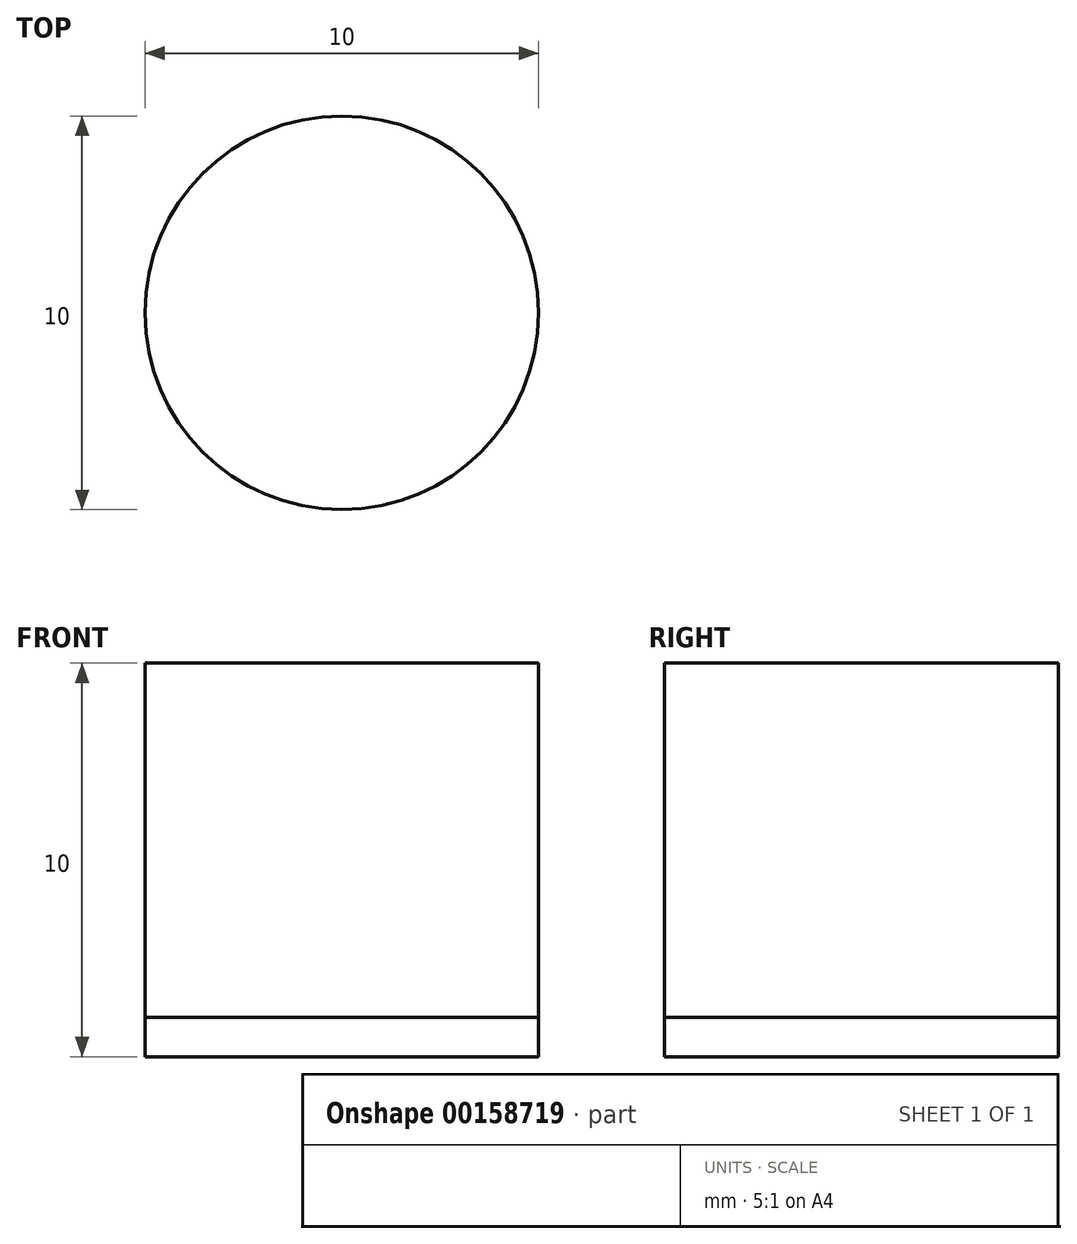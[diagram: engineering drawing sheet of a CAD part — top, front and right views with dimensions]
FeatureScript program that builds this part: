
annotation { "Feature Type Name" : "Feature", "Feature Type Description" : "" }
export const myFeature = defineFeature(function(context is Context, id is Id, definition is map)
    precondition{}
    {
        {
            var Q0;
            Q0=qCreatedBy(makeId("Top.planeOp"),FACE);
            var sketch = newSketch(context, id + "F0", { "sketchPlane" : qUnion([Q0])});
            skLineSegment(sketch, "E0.bottom", {"start": v(33, 33) * mm, "end": v(-33, 33) * mm});
            skLineSegment(sketch, "E0.top", {"start": v(33, -33) * mm, "end": v(-33, -33) * mm});
            skLineSegment(sketch, "E0.left", {"start": v(33, 33) * mm, "end": v(33, -33) * mm});
            skLineSegment(sketch, "E0.right", {"start": v(-33, 33) * mm, "end": v(-33, -33) * mm});
            skPoint(sketch, "E0.middle", {"position": v(0, 0) * mm});
            skCircle(sketch, "E1", {"center": v(-33, 33) * mm, "radius": 5 * mm});
            skCircle(sketch, "E2", {"center": v(-33, 33) * mm, "radius": 13 * mm});
            skCircle(sketch, "E3.0", {"center": v(-33, 33) * mm, "radius": 9 * mm});
            skCircle(sketch, "E4.0.1.0", {"center": v(-33, -33) * mm, "radius": 13 * mm});
            skCircle(sketch, "E4.0.1.1", {"center": v(-33, -33) * mm, "radius": 9 * mm});
            skCircle(sketch, "E4.0.1.2", {"center": v(-33, -33) * mm, "radius": 5 * mm});
            skCircle(sketch, "E4.1.0.0", {"center": v(33, 33) * mm, "radius": 13 * mm});
            skCircle(sketch, "E4.1.0.1", {"center": v(33, 33) * mm, "radius": 9 * mm});
            skCircle(sketch, "E4.1.0.2", {"center": v(33, 33) * mm, "radius": 5 * mm});
            skCircle(sketch, "E4.1.1.0", {"center": v(33, -33) * mm, "radius": 13 * mm});
            skCircle(sketch, "E4.1.1.1", {"center": v(33, -33) * mm, "radius": 9 * mm});
            skCircle(sketch, "E4.1.1.2", {"center": v(33, -33) * mm, "radius": 5 * mm});
            skLineSegment(sketch, "E4.direction1", {"start": v(-33, 33) * mm, "end": v(33, 33) * mm, "construction": true});
            skLineSegment(sketch, "E4.direction2", {"start": v(-33, 33) * mm, "end": v(-33, -33) * mm, "construction": true});
            skSolve(sketch);
        }
        {
            var Q0;
            {var subQ0=sQuery(id+"F0.wireOp",EDGE,"E2");var subQ1=sQuery(id+"F0.wireOp",EDGE,"E0.bottom");var subQ2=makeQuery(id+"F0.imprint","INTERSECT",VERTEX,{"derivedFrom":[subQ1,subQ0]});Q0=makeQuery(id+"F0.imprint","IMPRINT",FACE,{"disambiguationData":[TD([[makeQuery(id+"F0.imprint","IMPRINT",EDGE,{"disambiguationData":[TD([[subQ2,-1.0]])],"derivedFrom":subQ1}),-1.0]])]});}
            var Q1;
            {var subQ0=sQuery(id+"F0.wireOp",EDGE,"E2");var subQ1=sQuery(id+"F0.wireOp",EDGE,"E0.bottom");var subQ2=makeQuery(id+"F0.imprint","INTERSECT",VERTEX,{"derivedFrom":[subQ1,subQ0]});Q1=makeQuery(id+"F0.imprint","IMPRINT",FACE,{"disambiguationData":[TD([[makeQuery(id+"F0.imprint","IMPRINT",EDGE,{"disambiguationData":[TD([[subQ2,-1.0]])],"derivedFrom":subQ1}),1.0]])]});}
            extrude(context, id + "F1", {"entities" : qUnion([Q0, Q1]), "endBound" : BoundingType.SYMMETRIC, "depth" : 20 * mm});
        }
        {
            var Q0;
            {var subQ0=sQuery(id+"F0.wireOp",EDGE,"E3.0");var subQ1=sQuery(id+"F0.wireOp",EDGE,"E0.bottom");var subQ2=makeQuery(id+"F0.imprint","INTERSECT",VERTEX,{"derivedFrom":[subQ1,subQ0]});Q0=makeQuery(id+"F0.imprint","IMPRINT",FACE,{"disambiguationData":[TD([[makeQuery(id+"F0.imprint","IMPRINT",EDGE,{"disambiguationData":[TD([[subQ2,-1.0]])],"derivedFrom":subQ1}),-1.0]])]});}
            var Q1;
            {var subQ0=sQuery(id+"F0.wireOp",EDGE,"E3.0");var subQ1=sQuery(id+"F0.wireOp",EDGE,"E0.bottom");var subQ2=makeQuery(id+"F0.imprint","INTERSECT",VERTEX,{"derivedFrom":[subQ1,subQ0]});Q1=makeQuery(id+"F0.imprint","IMPRINT",FACE,{"disambiguationData":[TD([[makeQuery(id+"F0.imprint","IMPRINT",EDGE,{"disambiguationData":[TD([[subQ2,-1.0]])],"derivedFrom":subQ1}),1.0]])]});}
            extrude(context, id + "F2", {"entities" : qUnion([Q0, Q1]), "operationType" : NewBodyOperationType.ADD, "depth" : 5 * mm});
        }
        {
            var Q0;
            {var subQ0=sQuery(id+"F0.wireOp",EDGE,"E3.0");var subQ1=sQuery(id+"F0.wireOp",EDGE,"E0.bottom");var subQ2=makeQuery(id+"F0.imprint","INTERSECT",VERTEX,{"derivedFrom":[subQ1,subQ0]});Q0=makeQuery(id+"F0.imprint","IMPRINT",FACE,{"disambiguationData":[TD([[makeQuery(id+"F0.imprint","IMPRINT",EDGE,{"disambiguationData":[TD([[subQ2,-1.0]])],"derivedFrom":subQ1}),-1.0]])]});}
            var Q1;
            {var subQ0=sQuery(id+"F0.wireOp",EDGE,"E3.0");var subQ1=sQuery(id+"F0.wireOp",EDGE,"E0.bottom");var subQ2=makeQuery(id+"F0.imprint","INTERSECT",VERTEX,{"derivedFrom":[subQ1,subQ0]});Q1=makeQuery(id+"F0.imprint","IMPRINT",FACE,{"disambiguationData":[TD([[makeQuery(id+"F0.imprint","IMPRINT",EDGE,{"disambiguationData":[TD([[subQ2,-1.0]])],"derivedFrom":subQ1}),1.0]])]});}
            var Q2;
            Q2=makeQuery(id+"F1.opExtrude","CAP_FACE",FACE,{"disambiguationData":[OSD([sQuery(id+"F0.wireOp",EDGE,"E2"),sQuery(id+"F0.wireOp",EDGE,"E3.0")])],"isStart":true});
            extrude(context, id + "F3", {"entities" : qUnion([Q0, Q1]), "operationType" : NewBodyOperationType.ADD, "endBound" : BoundingType.UP_TO_SURFACE, "oppositeDirection" : true, "endBoundEntityFace" : qUnion([Q2]), "depth" : 10.25 * mm});
        }
        {
            var Q0;
            {var subQ0=sQuery(id+"F0.wireOp",EDGE,"E0.right");var subQ1=sQuery(id+"F0.wireOp",EDGE,"E0.bottom");var subQ2=makeQuery(id+"F0.imprint","INTERSECT",VERTEX,{"derivedFrom":[subQ1,subQ0]});Q0=makeQuery(id+"F0.imprint","IMPRINT",FACE,{"disambiguationData":[TD([[makeQuery(id+"F0.imprint","IMPRINT",EDGE,{"disambiguationData":[TD([[subQ2,1.0]])],"derivedFrom":subQ1}),-1.0]])]});}
            var Q1;
            {var subQ0=sQuery(id+"F0.wireOp",EDGE,"E0.right");var subQ1=sQuery(id+"F0.wireOp",EDGE,"E0.bottom");var subQ2=makeQuery(id+"F0.imprint","INTERSECT",VERTEX,{"derivedFrom":[subQ1,subQ0]});Q1=makeQuery(id+"F0.imprint","IMPRINT",FACE,{"disambiguationData":[TD([[makeQuery(id+"F0.imprint","IMPRINT",EDGE,{"disambiguationData":[TD([[subQ2,1.0]])],"derivedFrom":subQ1}),1.0]])]});}
            extrude(context, id + "F4", {"entities" : qUnion([Q0, Q1]), "operationType" : NewBodyOperationType.ADD, "depth" : 5 * mm});
        }
        {
            var Q0;
            {var subQ0=sQuery(id+"F0.wireOp",EDGE,"E0.right");var subQ1=sQuery(id+"F0.wireOp",EDGE,"E0.bottom");var subQ2=makeQuery(id+"F0.imprint","INTERSECT",VERTEX,{"derivedFrom":[subQ1,subQ0]});Q0=makeQuery(id+"F0.imprint","IMPRINT",FACE,{"disambiguationData":[TD([[makeQuery(id+"F0.imprint","IMPRINT",EDGE,{"disambiguationData":[TD([[subQ2,1.0]])],"derivedFrom":subQ1}),-1.0]])]});}
            var Q1;
            {var subQ0=sQuery(id+"F0.wireOp",EDGE,"E0.right");var subQ1=sQuery(id+"F0.wireOp",EDGE,"E0.bottom");var subQ2=makeQuery(id+"F0.imprint","INTERSECT",VERTEX,{"derivedFrom":[subQ1,subQ0]});Q1=makeQuery(id+"F0.imprint","IMPRINT",FACE,{"disambiguationData":[TD([[makeQuery(id+"F0.imprint","IMPRINT",EDGE,{"disambiguationData":[TD([[subQ2,1.0]])],"derivedFrom":subQ1}),1.0]])]});}
            extrude(context, id + "F5", {"entities" : qUnion([Q0, Q1]), "operationType" : NewBodyOperationType.ADD, "oppositeDirection" : true, "depth" : 9 * mm});
        }
        {
            var Q0;
            Q0=qCreatedBy(makeId("Top.planeOp"),FACE);
            var sketch = newSketch(context, id + "F6", { "sketchPlane" : qUnion([Q0])});
            skLineSegment(sketch, "E5.bottom", {"start": v(42, 42) * mm, "end": v(-42, 42) * mm});
            skLineSegment(sketch, "E5.top", {"start": v(42, -42) * mm, "end": v(-42, -42) * mm});
            skLineSegment(sketch, "E5.left", {"start": v(42, 42) * mm, "end": v(42, -42) * mm});
            skLineSegment(sketch, "E5.right", {"start": v(-42, 42) * mm, "end": v(-42, -42) * mm});
            skPoint(sketch, "E5.middle", {"position": v(0, 0) * mm});
            skFitSpline(sketch, "E6", {"points": [v(-42, 42) * mm, v(0, 48) * mm, v(42, 42) * mm], "startDerivative": vector(92.46, 24.65) * mm, "endDerivative": vector(96.06, -25.07) * mm});
            skFitSpline(sketch, "E7", {"points": [v(42, 42) * mm, v(48, 0) * mm, v(42, -42) * mm], "startDerivative": vector(24.84, -73.95) * mm, "endDerivative": vector(-21.58, -78.6) * mm});
            skFitSpline(sketch, "E8", {"points": [v(42, -42) * mm, v(0, -48) * mm, v(-42, -42) * mm], "startDerivative": vector(-77.44, -20.85) * mm, "endDerivative": vector(-75.53, 21.27) * mm});
            skFitSpline(sketch, "E9", {"points": [v(-42, -42) * mm, v(-48, 0) * mm, v(-42, 42) * mm], "startDerivative": vector(-24.73, 83.38) * mm, "endDerivative": vector(25.53, 85.94) * mm});
            skLineSegment(sketch, "E10.bottom", {"start": v(48, 48) * mm, "end": v(-48, 48) * mm});
            skLineSegment(sketch, "E10.top", {"start": v(48, -48) * mm, "end": v(-48, -48) * mm});
            skLineSegment(sketch, "E10.left", {"start": v(48, 48) * mm, "end": v(48, -48) * mm});
            skLineSegment(sketch, "E10.right", {"start": v(-48, 48) * mm, "end": v(-48, -48) * mm});
            skSolve(sketch);
        }
        {
            var Q0;
            Q0=qCreatedBy(makeId("Top.planeOp"),FACE);
            var sketch = newSketch(context, id + "F7", { "sketchPlane" : qUnion([Q0])});
            skLineSegment(sketch, "E11.bottom", {"start": v(28, 28) * mm, "end": v(-28, 28) * mm});
            skLineSegment(sketch, "E11.top", {"start": v(28, -28) * mm, "end": v(-28, -28) * mm});
            skLineSegment(sketch, "E11.left", {"start": v(28, 28) * mm, "end": v(28, -28) * mm});
            skLineSegment(sketch, "E11.right", {"start": v(-28, 28) * mm, "end": v(-28, -28) * mm});
            skPoint(sketch, "E11.middle", {"position": v(0, 0) * mm});
            skSolve(sketch);
        }
        {
            var Q0;
            {var subQ0=sQuery(id+"F0.wireOp",EDGE,"E4.1.0.0");var subQ1=sQuery(id+"F0.wireOp",EDGE,"E0.bottom");var subQ2=makeQuery(id+"F0.imprint","INTERSECT",VERTEX,{"derivedFrom":[subQ1,subQ0]});Q0=makeQuery(id+"F0.imprint","IMPRINT",FACE,{"disambiguationData":[TD([[makeQuery(id+"F0.imprint","IMPRINT",EDGE,{"disambiguationData":[TD([[subQ2,1.0]])],"derivedFrom":subQ1}),-1.0]])]});}
            var Q1;
            {var subQ0=sQuery(id+"F0.wireOp",EDGE,"E4.1.0.0");var subQ1=sQuery(id+"F0.wireOp",EDGE,"E0.bottom");var subQ2=makeQuery(id+"F0.imprint","INTERSECT",VERTEX,{"derivedFrom":[subQ1,subQ0]});Q1=makeQuery(id+"F0.imprint","IMPRINT",FACE,{"disambiguationData":[TD([[makeQuery(id+"F0.imprint","IMPRINT",EDGE,{"disambiguationData":[TD([[subQ2,1.0]])],"derivedFrom":subQ1}),1.0]])]});}
            extrude(context, id + "F8", {"entities" : qUnion([Q0, Q1]), "endBound" : BoundingType.SYMMETRIC, "depth" : 20 * mm});
        }
        {
            var Q0;
            {var subQ0=sQuery(id+"F0.wireOp",EDGE,"E4.1.0.2");var subQ1=sQuery(id+"F0.wireOp",EDGE,"E0.bottom");var subQ2=makeQuery(id+"F0.imprint","INTERSECT",VERTEX,{"derivedFrom":[subQ1,subQ0]});Q0=makeQuery(id+"F0.imprint","IMPRINT",FACE,{"disambiguationData":[TD([[makeQuery(id+"F0.imprint","IMPRINT",EDGE,{"disambiguationData":[TD([[subQ2,-1.0]])],"derivedFrom":subQ1}),1.0]])]});}
            var Q1;
            {var subQ0=sQuery(id+"F0.wireOp",EDGE,"E4.1.0.2");var subQ1=sQuery(id+"F0.wireOp",EDGE,"E0.bottom");var subQ2=makeQuery(id+"F0.imprint","INTERSECT",VERTEX,{"derivedFrom":[subQ1,subQ0]});Q1=makeQuery(id+"F0.imprint","IMPRINT",FACE,{"disambiguationData":[TD([[makeQuery(id+"F0.imprint","IMPRINT",EDGE,{"disambiguationData":[TD([[subQ2,-1.0]])],"derivedFrom":subQ1}),-1.0]])]});}
            extrude(context, id + "F9", {"entities" : qUnion([Q0, Q1]), "operationType" : NewBodyOperationType.ADD, "depth" : 5 * mm});
        }
        {
            var Q0;
            {var subQ0=sQuery(id+"F0.wireOp",EDGE,"E4.1.0.2");var subQ1=sQuery(id+"F0.wireOp",EDGE,"E0.bottom");var subQ2=makeQuery(id+"F0.imprint","INTERSECT",VERTEX,{"derivedFrom":[subQ1,subQ0]});Q0=makeQuery(id+"F0.imprint","IMPRINT",FACE,{"disambiguationData":[TD([[makeQuery(id+"F0.imprint","IMPRINT",EDGE,{"disambiguationData":[TD([[subQ2,-1.0]])],"derivedFrom":subQ1}),-1.0]])]});}
            var Q1;
            {var subQ0=sQuery(id+"F0.wireOp",EDGE,"E4.1.0.2");var subQ1=sQuery(id+"F0.wireOp",EDGE,"E0.bottom");var subQ2=makeQuery(id+"F0.imprint","INTERSECT",VERTEX,{"derivedFrom":[subQ1,subQ0]});Q1=makeQuery(id+"F0.imprint","IMPRINT",FACE,{"disambiguationData":[TD([[makeQuery(id+"F0.imprint","IMPRINT",EDGE,{"disambiguationData":[TD([[subQ2,-1.0]])],"derivedFrom":subQ1}),1.0]])]});}
            var Q2;
            Q2=makeQuery(id+"F8.opExtrude","CAP_FACE",FACE,{"disambiguationData":[OSD([sQuery(id+"F0.wireOp",EDGE,"E4.1.0.0"),sQuery(id+"F0.wireOp",EDGE,"E4.1.0.1")])],"isStart":true});
            extrude(context, id + "F10", {"entities" : qUnion([Q0, Q1]), "operationType" : NewBodyOperationType.ADD, "endBound" : BoundingType.UP_TO_SURFACE, "oppositeDirection" : true, "endBoundEntityFace" : qUnion([Q2]), "depth" : 25 * mm});
        }
        {
            var Q0;
            {var subQ0=sQuery(id+"F0.wireOp",EDGE,"E0.left");var subQ1=sQuery(id+"F0.wireOp",EDGE,"E0.bottom");var subQ2=makeQuery(id+"F0.imprint","INTERSECT",VERTEX,{"derivedFrom":[subQ1,subQ0]});Q0=makeQuery(id+"F0.imprint","IMPRINT",FACE,{"disambiguationData":[TD([[makeQuery(id+"F0.imprint","IMPRINT",EDGE,{"disambiguationData":[TD([[subQ2,-1.0]])],"derivedFrom":subQ1}),-1.0]])]});}
            var Q1;
            {var subQ0=sQuery(id+"F0.wireOp",EDGE,"E0.left");var subQ1=sQuery(id+"F0.wireOp",EDGE,"E0.bottom");var subQ2=makeQuery(id+"F0.imprint","INTERSECT",VERTEX,{"derivedFrom":[subQ1,subQ0]});Q1=makeQuery(id+"F0.imprint","IMPRINT",FACE,{"disambiguationData":[TD([[makeQuery(id+"F0.imprint","IMPRINT",EDGE,{"disambiguationData":[TD([[subQ2,-1.0]])],"derivedFrom":subQ1}),1.0]])]});}
            extrude(context, id + "F11", {"entities" : qUnion([Q0, Q1]), "operationType" : NewBodyOperationType.ADD, "oppositeDirection" : true, "depth" : 9 * mm});
        }
        {
            var Q0;
            {var subQ0=sQuery(id+"F0.wireOp",EDGE,"E0.left");var subQ1=sQuery(id+"F0.wireOp",EDGE,"E0.bottom");var subQ2=makeQuery(id+"F0.imprint","INTERSECT",VERTEX,{"derivedFrom":[subQ1,subQ0]});Q0=makeQuery(id+"F0.imprint","IMPRINT",FACE,{"disambiguationData":[TD([[makeQuery(id+"F0.imprint","IMPRINT",EDGE,{"disambiguationData":[TD([[subQ2,-1.0]])],"derivedFrom":subQ1}),-1.0]])]});}
            var Q1;
            {var subQ0=sQuery(id+"F0.wireOp",EDGE,"E0.left");var subQ1=sQuery(id+"F0.wireOp",EDGE,"E0.bottom");var subQ2=makeQuery(id+"F0.imprint","INTERSECT",VERTEX,{"derivedFrom":[subQ1,subQ0]});Q1=makeQuery(id+"F0.imprint","IMPRINT",FACE,{"disambiguationData":[TD([[makeQuery(id+"F0.imprint","IMPRINT",EDGE,{"disambiguationData":[TD([[subQ2,-1.0]])],"derivedFrom":subQ1}),1.0]])]});}
            var Q2;
            Q2=makeQuery(id+"F9.opExtrude","CAP_FACE",FACE,{"disambiguationData":[OSD([sQuery(id+"F0.wireOp",EDGE,"E4.1.0.1"),sQuery(id+"F0.wireOp",EDGE,"E4.1.0.2")])],"isStart":false});
            extrude(context, id + "F12", {"entities" : qUnion([Q0, Q1]), "operationType" : NewBodyOperationType.ADD, "endBound" : BoundingType.UP_TO_SURFACE, "endBoundEntityFace" : qUnion([Q2]), "depth" : 25 * mm});
        }
        {
            var Q0;
            {var subQ0=sQuery(id+"F0.wireOp",EDGE,"E4.0.1.0");var subQ1=sQuery(id+"F0.wireOp",EDGE,"E0.top");var subQ2=makeQuery(id+"F0.imprint","INTERSECT",VERTEX,{"derivedFrom":[subQ1,subQ0]});Q0=makeQuery(id+"F0.imprint","IMPRINT",FACE,{"disambiguationData":[TD([[makeQuery(id+"F0.imprint","IMPRINT",EDGE,{"disambiguationData":[TD([[subQ2,-1.0]])],"derivedFrom":subQ1}),1.0]])]});}
            var Q1;
            {var subQ0=sQuery(id+"F0.wireOp",EDGE,"E4.0.1.0");var subQ1=sQuery(id+"F0.wireOp",EDGE,"E0.top");var subQ2=makeQuery(id+"F0.imprint","INTERSECT",VERTEX,{"derivedFrom":[subQ1,subQ0]});Q1=makeQuery(id+"F0.imprint","IMPRINT",FACE,{"disambiguationData":[TD([[makeQuery(id+"F0.imprint","IMPRINT",EDGE,{"disambiguationData":[TD([[subQ2,-1.0]])],"derivedFrom":subQ1}),-1.0]])]});}
            extrude(context, id + "F13", {"entities" : qUnion([Q0, Q1]), "endBound" : BoundingType.SYMMETRIC, "depth" : 20 * mm});
        }
        {
            var Q0;
            {var subQ0=sQuery(id+"F0.wireOp",EDGE,"E4.0.1.1");var subQ1=sQuery(id+"F0.wireOp",EDGE,"E0.top");var subQ2=makeQuery(id+"F0.imprint","INTERSECT",VERTEX,{"derivedFrom":[subQ1,subQ0]});Q0=makeQuery(id+"F0.imprint","IMPRINT",FACE,{"disambiguationData":[TD([[makeQuery(id+"F0.imprint","IMPRINT",EDGE,{"disambiguationData":[TD([[subQ2,-1.0]])],"derivedFrom":subQ1}),1.0]])]});}
            var Q1;
            {var subQ0=sQuery(id+"F0.wireOp",EDGE,"E4.0.1.1");var subQ1=sQuery(id+"F0.wireOp",EDGE,"E0.top");var subQ2=makeQuery(id+"F0.imprint","INTERSECT",VERTEX,{"derivedFrom":[subQ1,subQ0]});Q1=makeQuery(id+"F0.imprint","IMPRINT",FACE,{"disambiguationData":[TD([[makeQuery(id+"F0.imprint","IMPRINT",EDGE,{"disambiguationData":[TD([[subQ2,-1.0]])],"derivedFrom":subQ1}),-1.0]])]});}
            extrude(context, id + "F14", {"entities" : qUnion([Q0, Q1]), "operationType" : NewBodyOperationType.ADD, "depth" : 5 * mm});
        }
        {
            var Q0;
            {var subQ0=sQuery(id+"F0.wireOp",EDGE,"E4.0.1.1");var subQ1=sQuery(id+"F0.wireOp",EDGE,"E0.top");var subQ2=makeQuery(id+"F0.imprint","INTERSECT",VERTEX,{"derivedFrom":[subQ1,subQ0]});Q0=makeQuery(id+"F0.imprint","IMPRINT",FACE,{"disambiguationData":[TD([[makeQuery(id+"F0.imprint","IMPRINT",EDGE,{"disambiguationData":[TD([[subQ2,-1.0]])],"derivedFrom":subQ1}),1.0]])]});}
            var Q1;
            {var subQ0=sQuery(id+"F0.wireOp",EDGE,"E4.0.1.1");var subQ1=sQuery(id+"F0.wireOp",EDGE,"E0.top");var subQ2=makeQuery(id+"F0.imprint","INTERSECT",VERTEX,{"derivedFrom":[subQ1,subQ0]});Q1=makeQuery(id+"F0.imprint","IMPRINT",FACE,{"disambiguationData":[TD([[makeQuery(id+"F0.imprint","IMPRINT",EDGE,{"disambiguationData":[TD([[subQ2,-1.0]])],"derivedFrom":subQ1}),-1.0]])]});}
            var Q2;
            Q2=makeQuery(id+"F13.opExtrude","CAP_FACE",FACE,{"disambiguationData":[OSD([sQuery(id+"F0.wireOp",EDGE,"E4.0.1.0"),sQuery(id+"F0.wireOp",EDGE,"E4.0.1.1")])],"isStart":true});
            extrude(context, id + "F15", {"entities" : qUnion([Q0, Q1]), "operationType" : NewBodyOperationType.ADD, "endBound" : BoundingType.UP_TO_SURFACE, "oppositeDirection" : true, "endBoundEntityFace" : qUnion([Q2]), "depth" : 25 * mm});
        }
        {
            var Q0;
            {var subQ0=sQuery(id+"F0.wireOp",EDGE,"E0.right");var subQ1=sQuery(id+"F0.wireOp",EDGE,"E0.top");var subQ2=makeQuery(id+"F0.imprint","INTERSECT",VERTEX,{"derivedFrom":[subQ1,subQ0]});Q0=makeQuery(id+"F0.imprint","IMPRINT",FACE,{"disambiguationData":[TD([[makeQuery(id+"F0.imprint","IMPRINT",EDGE,{"disambiguationData":[TD([[subQ2,1.0]])],"derivedFrom":subQ1}),1.0]])]});}
            var Q1;
            {var subQ0=sQuery(id+"F0.wireOp",EDGE,"E0.right");var subQ1=sQuery(id+"F0.wireOp",EDGE,"E0.top");var subQ2=makeQuery(id+"F0.imprint","INTERSECT",VERTEX,{"derivedFrom":[subQ1,subQ0]});Q1=makeQuery(id+"F0.imprint","IMPRINT",FACE,{"disambiguationData":[TD([[makeQuery(id+"F0.imprint","IMPRINT",EDGE,{"disambiguationData":[TD([[subQ2,1.0]])],"derivedFrom":subQ1}),-1.0]])]});}
            extrude(context, id + "F16", {"entities" : qUnion([Q0, Q1]), "operationType" : NewBodyOperationType.ADD, "oppositeDirection" : true, "depth" : 9 * mm});
        }
        {
            var Q0;
            {var subQ0=sQuery(id+"F0.wireOp",EDGE,"E0.right");var subQ1=sQuery(id+"F0.wireOp",EDGE,"E0.top");var subQ2=makeQuery(id+"F0.imprint","INTERSECT",VERTEX,{"derivedFrom":[subQ1,subQ0]});Q0=makeQuery(id+"F0.imprint","IMPRINT",FACE,{"disambiguationData":[TD([[makeQuery(id+"F0.imprint","IMPRINT",EDGE,{"disambiguationData":[TD([[subQ2,1.0]])],"derivedFrom":subQ1}),1.0]])]});}
            var Q1;
            {var subQ0=sQuery(id+"F0.wireOp",EDGE,"E0.right");var subQ1=sQuery(id+"F0.wireOp",EDGE,"E0.top");var subQ2=makeQuery(id+"F0.imprint","INTERSECT",VERTEX,{"derivedFrom":[subQ1,subQ0]});Q1=makeQuery(id+"F0.imprint","IMPRINT",FACE,{"disambiguationData":[TD([[makeQuery(id+"F0.imprint","IMPRINT",EDGE,{"disambiguationData":[TD([[subQ2,1.0]])],"derivedFrom":subQ1}),-1.0]])]});}
            var Q2;
            Q2=makeQuery(id+"F14.opExtrude","CAP_FACE",FACE,{"disambiguationData":[OSD([sQuery(id+"F0.wireOp",EDGE,"E4.0.1.1"),sQuery(id+"F0.wireOp",EDGE,"E4.0.1.2")])],"isStart":false});
            extrude(context, id + "F17", {"entities" : qUnion([Q0, Q1]), "operationType" : NewBodyOperationType.ADD, "endBound" : BoundingType.UP_TO_SURFACE, "endBoundEntityFace" : qUnion([Q2]), "depth" : 25 * mm});
        }
        {
            var Q0;
            {var subQ0=sQuery(id+"F0.wireOp",EDGE,"E4.1.1.0");var subQ1=sQuery(id+"F0.wireOp",EDGE,"E0.top");var subQ2=makeQuery(id+"F0.imprint","INTERSECT",VERTEX,{"derivedFrom":[subQ1,subQ0]});Q0=makeQuery(id+"F0.imprint","IMPRINT",FACE,{"disambiguationData":[TD([[makeQuery(id+"F0.imprint","IMPRINT",EDGE,{"disambiguationData":[TD([[subQ2,1.0]])],"derivedFrom":subQ1}),1.0]])]});}
            var Q1;
            {var subQ0=sQuery(id+"F0.wireOp",EDGE,"E4.1.1.0");var subQ1=sQuery(id+"F0.wireOp",EDGE,"E0.top");var subQ2=makeQuery(id+"F0.imprint","INTERSECT",VERTEX,{"derivedFrom":[subQ1,subQ0]});Q1=makeQuery(id+"F0.imprint","IMPRINT",FACE,{"disambiguationData":[TD([[makeQuery(id+"F0.imprint","IMPRINT",EDGE,{"disambiguationData":[TD([[subQ2,1.0]])],"derivedFrom":subQ1}),-1.0]])]});}
            extrude(context, id + "F18", {"entities" : qUnion([Q0, Q1]), "endBound" : BoundingType.SYMMETRIC, "depth" : 20 * mm});
        }
        {
            var Q0;
            {var subQ0=sQuery(id+"F0.wireOp",EDGE,"E4.1.1.2");var subQ1=sQuery(id+"F0.wireOp",EDGE,"E0.top");var subQ2=makeQuery(id+"F0.imprint","INTERSECT",VERTEX,{"derivedFrom":[subQ1,subQ0]});Q0=makeQuery(id+"F0.imprint","IMPRINT",FACE,{"disambiguationData":[TD([[makeQuery(id+"F0.imprint","IMPRINT",EDGE,{"disambiguationData":[TD([[subQ2,-1.0]])],"derivedFrom":subQ1}),1.0]])]});}
            var Q1;
            {var subQ0=sQuery(id+"F0.wireOp",EDGE,"E4.1.1.2");var subQ1=sQuery(id+"F0.wireOp",EDGE,"E0.top");var subQ2=makeQuery(id+"F0.imprint","INTERSECT",VERTEX,{"derivedFrom":[subQ1,subQ0]});Q1=makeQuery(id+"F0.imprint","IMPRINT",FACE,{"disambiguationData":[TD([[makeQuery(id+"F0.imprint","IMPRINT",EDGE,{"disambiguationData":[TD([[subQ2,-1.0]])],"derivedFrom":subQ1}),-1.0]])]});}
            extrude(context, id + "F19", {"entities" : qUnion([Q0, Q1]), "operationType" : NewBodyOperationType.ADD, "depth" : 5 * mm});
        }
        {
            var Q0;
            {var subQ0=sQuery(id+"F0.wireOp",EDGE,"E4.1.1.2");var subQ1=sQuery(id+"F0.wireOp",EDGE,"E0.top");var subQ2=makeQuery(id+"F0.imprint","INTERSECT",VERTEX,{"derivedFrom":[subQ1,subQ0]});Q0=makeQuery(id+"F0.imprint","IMPRINT",FACE,{"disambiguationData":[TD([[makeQuery(id+"F0.imprint","IMPRINT",EDGE,{"disambiguationData":[TD([[subQ2,-1.0]])],"derivedFrom":subQ1}),1.0]])]});}
            var Q1;
            {var subQ0=sQuery(id+"F0.wireOp",EDGE,"E4.1.1.2");var subQ1=sQuery(id+"F0.wireOp",EDGE,"E0.top");var subQ2=makeQuery(id+"F0.imprint","INTERSECT",VERTEX,{"derivedFrom":[subQ1,subQ0]});Q1=makeQuery(id+"F0.imprint","IMPRINT",FACE,{"disambiguationData":[TD([[makeQuery(id+"F0.imprint","IMPRINT",EDGE,{"disambiguationData":[TD([[subQ2,-1.0]])],"derivedFrom":subQ1}),-1.0]])]});}
            var Q2;
            Q2=makeQuery(id+"F18.opExtrude","CAP_FACE",FACE,{"disambiguationData":[OSD([sQuery(id+"F0.wireOp",EDGE,"E4.1.1.0"),sQuery(id+"F0.wireOp",EDGE,"E4.1.1.1")])],"isStart":true});
            extrude(context, id + "F20", {"entities" : qUnion([Q0, Q1]), "operationType" : NewBodyOperationType.ADD, "endBound" : BoundingType.UP_TO_SURFACE, "oppositeDirection" : true, "endBoundEntityFace" : qUnion([Q2]), "depth" : 25 * mm});
        }
        {
            var Q0;
            {var subQ0=sQuery(id+"F0.wireOp",EDGE,"E0.left");var subQ1=sQuery(id+"F0.wireOp",EDGE,"E0.top");var subQ2=makeQuery(id+"F0.imprint","INTERSECT",VERTEX,{"derivedFrom":[subQ1,subQ0]});Q0=makeQuery(id+"F0.imprint","IMPRINT",FACE,{"disambiguationData":[TD([[makeQuery(id+"F0.imprint","IMPRINT",EDGE,{"disambiguationData":[TD([[subQ2,-1.0]])],"derivedFrom":subQ1}),1.0]])]});}
            var Q1;
            {var subQ0=sQuery(id+"F0.wireOp",EDGE,"E0.left");var subQ1=sQuery(id+"F0.wireOp",EDGE,"E0.top");var subQ2=makeQuery(id+"F0.imprint","INTERSECT",VERTEX,{"derivedFrom":[subQ1,subQ0]});Q1=makeQuery(id+"F0.imprint","IMPRINT",FACE,{"disambiguationData":[TD([[makeQuery(id+"F0.imprint","IMPRINT",EDGE,{"disambiguationData":[TD([[subQ2,-1.0]])],"derivedFrom":subQ1}),-1.0]])]});}
            extrude(context, id + "F21", {"entities" : qUnion([Q0, Q1]), "operationType" : NewBodyOperationType.ADD, "oppositeDirection" : true, "depth" : 9 * mm});
        }
        {
            var Q0;
            {var subQ0=sQuery(id+"F0.wireOp",EDGE,"E0.left");var subQ1=sQuery(id+"F0.wireOp",EDGE,"E0.top");var subQ2=makeQuery(id+"F0.imprint","INTERSECT",VERTEX,{"derivedFrom":[subQ1,subQ0]});Q0=makeQuery(id+"F0.imprint","IMPRINT",FACE,{"disambiguationData":[TD([[makeQuery(id+"F0.imprint","IMPRINT",EDGE,{"disambiguationData":[TD([[subQ2,-1.0]])],"derivedFrom":subQ1}),1.0]])]});}
            var Q1;
            {var subQ0=sQuery(id+"F0.wireOp",EDGE,"E0.left");var subQ1=sQuery(id+"F0.wireOp",EDGE,"E0.top");var subQ2=makeQuery(id+"F0.imprint","INTERSECT",VERTEX,{"derivedFrom":[subQ1,subQ0]});Q1=makeQuery(id+"F0.imprint","IMPRINT",FACE,{"disambiguationData":[TD([[makeQuery(id+"F0.imprint","IMPRINT",EDGE,{"disambiguationData":[TD([[subQ2,-1.0]])],"derivedFrom":subQ1}),-1.0]])]});}
            var Q2;
            Q2=makeQuery(id+"F19.opExtrude","CAP_FACE",FACE,{"disambiguationData":[OSD([sQuery(id+"F0.wireOp",EDGE,"E4.1.1.1"),sQuery(id+"F0.wireOp",EDGE,"E4.1.1.2")])],"isStart":false});
            extrude(context, id + "F22", {"entities" : qUnion([Q0, Q1]), "operationType" : NewBodyOperationType.ADD, "endBound" : BoundingType.UP_TO_SURFACE, "endBoundEntityFace" : qUnion([Q2]), "depth" : 25 * mm});
        }
        {
            var Q0;
            Q0=makeQuery(id+"F6.imprint","IMPRINT",FACE,{"disambiguationData":[TD([[makeQuery(id+"F6.imprint","IMPRINT",EDGE,{"derivedFrom":sQuery(id+"F6.wireOp",EDGE,"E5.bottom")}),1.0]])]});
            var Q1;
            {var subQ0=sQuery(id+"F6.wireOp",EDGE,"E5.right");Q1=makeQuery(id+"F6.imprint","IMPRINT",FACE,{"disambiguationData":[TD([[makeQuery(id+"F6.imprint","IMPRINT",EDGE,{"derivedFrom":subQ0}),-1.0]])]});}
            var Q2;
            {var subQ0=sQuery(id+"F6.wireOp",EDGE,"E5.top");Q2=makeQuery(id+"F6.imprint","IMPRINT",FACE,{"disambiguationData":[TD([[makeQuery(id+"F6.imprint","IMPRINT",EDGE,{"derivedFrom":subQ0}),1.0]])]});}
            var Q3;
            {var subQ0=sQuery(id+"F6.wireOp",EDGE,"E5.left");Q3=makeQuery(id+"F6.imprint","IMPRINT",FACE,{"disambiguationData":[TD([[makeQuery(id+"F6.imprint","IMPRINT",EDGE,{"derivedFrom":subQ0}),1.0]])]});}
            var Q4;
            {var subQ0=sQuery(id+"F6.wireOp",EDGE,"E5.bottom");Q4=makeQuery(id+"F6.imprint","IMPRINT",FACE,{"disambiguationData":[TD([[makeQuery(id+"F6.imprint","IMPRINT",EDGE,{"derivedFrom":subQ0}),-1.0]])]});}
            var Q5;
            {var subQ0=sQuery(id+"F0.wireOp",EDGE,"E4.0.1.1");Q5=makeQuery(id+"F15.boolean.opBoolean","MERGE",FACE,{"derivedFrom":[makeQuery(id+"F13.opExtrude","CAP_FACE",FACE,{"disambiguationData":[OSD([sQuery(id+"F0.wireOp",EDGE,"E4.0.1.0"),subQ0])],"isStart":true}),makeQuery(id+"F15.opExtrude","CAP_FACE",FACE,{"disambiguationData":[OSD([subQ0,sQuery(id+"F0.wireOp",EDGE,"E4.0.1.2")])],"isStart":false})]});}
            extrude(context, id + "F23", {"entities" : qUnion([Q0, Q1, Q2, Q3, Q4]), "endBound" : BoundingType.UP_TO_SURFACE, "oppositeDirection" : true, "endBoundEntityFace" : qUnion([Q5]), "depth" : 25 * mm});
        }
        {
            var Q0;
            Q0=makeQuery(id+"F6.imprint","IMPRINT",FACE,{"disambiguationData":[TD([[makeQuery(id+"F6.imprint","IMPRINT",EDGE,{"derivedFrom":sQuery(id+"F6.wireOp",EDGE,"E5.bottom")}),1.0]])]});
            var Q1;
            {var subQ0=sQuery(id+"F6.wireOp",EDGE,"E5.right");Q1=makeQuery(id+"F6.imprint","IMPRINT",FACE,{"disambiguationData":[TD([[makeQuery(id+"F6.imprint","IMPRINT",EDGE,{"derivedFrom":subQ0}),-1.0]])]});}
            var Q2;
            {var subQ0=sQuery(id+"F6.wireOp",EDGE,"E5.top");Q2=makeQuery(id+"F6.imprint","IMPRINT",FACE,{"disambiguationData":[TD([[makeQuery(id+"F6.imprint","IMPRINT",EDGE,{"derivedFrom":subQ0}),1.0]])]});}
            var Q3;
            {var subQ0=sQuery(id+"F6.wireOp",EDGE,"E5.left");Q3=makeQuery(id+"F6.imprint","IMPRINT",FACE,{"disambiguationData":[TD([[makeQuery(id+"F6.imprint","IMPRINT",EDGE,{"derivedFrom":subQ0}),1.0]])]});}
            var Q4;
            {var subQ0=sQuery(id+"F6.wireOp",EDGE,"E5.bottom");Q4=makeQuery(id+"F6.imprint","IMPRINT",FACE,{"disambiguationData":[TD([[makeQuery(id+"F6.imprint","IMPRINT",EDGE,{"derivedFrom":subQ0}),-1.0]])]});}
            var Q5;
            {var subQ0=sQuery(id+"F0.wireOp",EDGE,"E4.1.0.2");Q5=makeQuery(id+"F12.boolean.opBoolean","MERGE",FACE,{"derivedFrom":[makeQuery(id+"F9.opExtrude","CAP_FACE",FACE,{"disambiguationData":[OSD([sQuery(id+"F0.wireOp",EDGE,"E4.1.0.1"),subQ0])],"isStart":false}),makeQuery(id+"F12.opExtrude","CAP_FACE",FACE,{"disambiguationData":[OSD([subQ0])],"isStart":false})]});}
            extrude(context, id + "F24", {"entities" : qUnion([Q0, Q1, Q2, Q3, Q4]), "endBound" : BoundingType.UP_TO_SURFACE, "endBoundEntityFace" : qUnion([Q5]), "depth" : 25 * mm});
        }
        {
            var Q0;
            Q0=makeQuery(id+"F7.imprint","IMPRINT",FACE,{"disambiguationData":[TD([[makeQuery(id+"F7.imprint","IMPRINT",EDGE,{"derivedFrom":sQuery(id+"F7.wireOp",EDGE,"E11.bottom")}),1.0]])]});
            extrude(context, id + "F25", {"entities" : qUnion([Q0]), "operationType" : NewBodyOperationType.REMOVE, "endBound" : BoundingType.SYMMETRIC, "oppositeDirection" : true, "depth" : 25 * mm});
        }
        {
            var Q0;
            Q0=makeQuery(id+"F7.imprint","IMPRINT",FACE,{"disambiguationData":[TD([[makeQuery(id+"F7.imprint","IMPRINT",EDGE,{"derivedFrom":sQuery(id+"F7.wireOp",EDGE,"E11.bottom")}),1.0]])]});
            extrude(context, id + "F26", {"entities" : qUnion([Q0]), "operationType" : NewBodyOperationType.REMOVE, "endBound" : BoundingType.SYMMETRIC, "depth" : 25 * mm});
        }
        {
            var Q0;
            Q0=makeQuery(id+"F18.opExtrude","CAP_EDGE",EDGE,{"disambiguationData":[OSD([sQuery(id+"F0.wireOp",EDGE,"E4.1.1.0")])],"isStart":true});
            var Q1;
            Q1=makeQuery(id+"F13.opExtrude","CAP_EDGE",EDGE,{"disambiguationData":[OSD([sQuery(id+"F0.wireOp",EDGE,"E4.0.1.0")])],"isStart":true});
            var Q2;
            Q2=makeQuery(id+"F8.opExtrude","CAP_EDGE",EDGE,{"disambiguationData":[OSD([sQuery(id+"F0.wireOp",EDGE,"E4.1.0.0")])],"isStart":true});
            var Q3;
            Q3=makeQuery(id+"F1.opExtrude","CAP_EDGE",EDGE,{"disambiguationData":[OSD([sQuery(id+"F0.wireOp",EDGE,"E2")])],"isStart":true});
            fillet(context, id + "F27", {"entities" : qUnion([Q0, Q1, Q2, Q3]), "radius" : 2 * mm, "tangentPropagation" : true, "allowEdgeOverflow" : false});
        }
        {
            var Q0;
            {var subQ0=sQuery(id+"F6.wireOp",EDGE,"E9");Q0=makeQuery(id+"F24.opExtrude","CAP_EDGE",EDGE,{"disambiguationData":[OSD([subQ0]),TDD([makeQuery(id+"F6.imprint","IMPRINT",EDGE,{"disambiguationData":[TD([[makeQuery(id+"F6.imprint","INTERSECT",VERTEX,{"disambiguationData":[OD(1.0)],"derivedFrom":[subQ0,sQuery(id+"F6.wireOp",EDGE,"E10.right")]}),-1.0]])],"derivedFrom":subQ0})])],"isStart":false});}
            var Q1;
            {var subQ0=sQuery(id+"F6.wireOp",EDGE,"E9");Q1=makeQuery(id+"F24.opExtrude","CAP_EDGE",EDGE,{"disambiguationData":[OSD([subQ0]),TDD([makeQuery(id+"F6.imprint","IMPRINT",EDGE,{"disambiguationData":[TD([[makeQuery(id+"F6.imprint","INTERSECT",VERTEX,{"disambiguationData":[OD(0.0)],"derivedFrom":[subQ0,sQuery(id+"F6.wireOp",EDGE,"E10.right")]}),1.0]])],"derivedFrom":subQ0})])],"isStart":false});}
            var Q2;
            {var subQ0=sQuery(id+"F6.wireOp",EDGE,"E8");Q2=makeQuery(id+"F24.opExtrude","CAP_EDGE",EDGE,{"disambiguationData":[OSD([subQ0]),TDD([makeQuery(id+"F6.imprint","IMPRINT",EDGE,{"disambiguationData":[TD([[makeQuery(id+"F6.imprint","INTERSECT",VERTEX,{"disambiguationData":[OD(1.0)],"derivedFrom":[subQ0,sQuery(id+"F6.wireOp",EDGE,"E10.top")]}),-1.0]])],"derivedFrom":subQ0})])],"isStart":false});}
            var Q3;
            {var subQ0=sQuery(id+"F6.wireOp",EDGE,"E8");Q3=makeQuery(id+"F24.opExtrude","CAP_EDGE",EDGE,{"disambiguationData":[OSD([subQ0]),TDD([makeQuery(id+"F6.imprint","IMPRINT",EDGE,{"disambiguationData":[TD([[makeQuery(id+"F6.imprint","INTERSECT",VERTEX,{"disambiguationData":[OD(0.0)],"derivedFrom":[subQ0,sQuery(id+"F6.wireOp",EDGE,"E10.top")]}),1.0]])],"derivedFrom":subQ0})])],"isStart":false});}
            var Q4;
            {var subQ0=sQuery(id+"F6.wireOp",EDGE,"E7");Q4=makeQuery(id+"F24.opExtrude","CAP_EDGE",EDGE,{"disambiguationData":[OSD([subQ0]),TDD([makeQuery(id+"F6.imprint","IMPRINT",EDGE,{"disambiguationData":[TD([[makeQuery(id+"F6.imprint","INTERSECT",VERTEX,{"disambiguationData":[OD(1.0)],"derivedFrom":[subQ0,sQuery(id+"F6.wireOp",EDGE,"E10.left")]}),-1.0]])],"derivedFrom":subQ0})])],"isStart":false});}
            var Q5;
            {var subQ0=sQuery(id+"F6.wireOp",EDGE,"E7");Q5=makeQuery(id+"F24.opExtrude","CAP_EDGE",EDGE,{"disambiguationData":[OSD([subQ0]),TDD([makeQuery(id+"F6.imprint","IMPRINT",EDGE,{"disambiguationData":[TD([[makeQuery(id+"F6.imprint","INTERSECT",VERTEX,{"disambiguationData":[OD(0.0)],"derivedFrom":[subQ0,sQuery(id+"F6.wireOp",EDGE,"E10.left")]}),1.0]])],"derivedFrom":subQ0})])],"isStart":false});}
            var Q6;
            {var subQ0=sQuery(id+"F6.wireOp",EDGE,"E6");Q6=makeQuery(id+"F24.opExtrude","CAP_EDGE",EDGE,{"disambiguationData":[OSD([subQ0]),TDD([makeQuery(id+"F6.imprint","IMPRINT",EDGE,{"disambiguationData":[TD([[makeQuery(id+"F6.imprint","INTERSECT",VERTEX,{"disambiguationData":[OD(1.0)],"derivedFrom":[subQ0,sQuery(id+"F6.wireOp",EDGE,"E10.bottom")]}),-1.0]])],"derivedFrom":subQ0})])],"isStart":false});}
            var Q7;
            {var subQ0=sQuery(id+"F6.wireOp",EDGE,"E6");Q7=makeQuery(id+"F24.opExtrude","CAP_EDGE",EDGE,{"disambiguationData":[OSD([subQ0]),TDD([makeQuery(id+"F6.imprint","IMPRINT",EDGE,{"disambiguationData":[TD([[makeQuery(id+"F6.imprint","INTERSECT",VERTEX,{"disambiguationData":[OD(0.0)],"derivedFrom":[subQ0,sQuery(id+"F6.wireOp",EDGE,"E10.bottom")]}),1.0]])],"derivedFrom":subQ0})])],"isStart":false});}
            fillet(context, id + "F28", {"entities" : qUnion([Q0, Q1, Q2, Q3, Q4, Q5, Q6, Q7]), "radius" : 3 * mm, "tangentPropagation" : true, "allowEdgeOverflow" : false});
        }
        {
            var Q0;
            {var subQ0=sQuery(id+"F6.wireOp",EDGE,"E9");Q0=makeQuery(id+"F23.opExtrude","CAP_EDGE",EDGE,{"disambiguationData":[OSD([subQ0]),TDD([makeQuery(id+"F6.imprint","IMPRINT",EDGE,{"disambiguationData":[TD([[makeQuery(id+"F6.imprint","INTERSECT",VERTEX,{"disambiguationData":[OD(0.0)],"derivedFrom":[subQ0,sQuery(id+"F6.wireOp",EDGE,"E10.right")]}),1.0]])],"derivedFrom":subQ0})])],"isStart":false});}
            var Q1;
            {var subQ0=sQuery(id+"F6.wireOp",EDGE,"E9");Q1=makeQuery(id+"F23.opExtrude","CAP_EDGE",EDGE,{"disambiguationData":[OSD([subQ0]),TDD([makeQuery(id+"F6.imprint","IMPRINT",EDGE,{"disambiguationData":[TD([[makeQuery(id+"F6.imprint","INTERSECT",VERTEX,{"disambiguationData":[OD(1.0)],"derivedFrom":[subQ0,sQuery(id+"F6.wireOp",EDGE,"E10.right")]}),-1.0]])],"derivedFrom":subQ0})])],"isStart":false});}
            var Q2;
            {var subQ0=sQuery(id+"F6.wireOp",EDGE,"E6");Q2=makeQuery(id+"F23.opExtrude","CAP_EDGE",EDGE,{"disambiguationData":[OSD([subQ0]),TDD([makeQuery(id+"F6.imprint","IMPRINT",EDGE,{"disambiguationData":[TD([[makeQuery(id+"F6.imprint","INTERSECT",VERTEX,{"disambiguationData":[OD(0.0)],"derivedFrom":[subQ0,sQuery(id+"F6.wireOp",EDGE,"E10.bottom")]}),1.0]])],"derivedFrom":subQ0})])],"isStart":false});}
            var Q3;
            {var subQ0=sQuery(id+"F6.wireOp",EDGE,"E6");Q3=makeQuery(id+"F23.opExtrude","CAP_EDGE",EDGE,{"disambiguationData":[OSD([subQ0]),TDD([makeQuery(id+"F6.imprint","IMPRINT",EDGE,{"disambiguationData":[TD([[makeQuery(id+"F6.imprint","INTERSECT",VERTEX,{"disambiguationData":[OD(1.0)],"derivedFrom":[subQ0,sQuery(id+"F6.wireOp",EDGE,"E10.bottom")]}),-1.0]])],"derivedFrom":subQ0})])],"isStart":false});}
            var Q4;
            {var subQ0=sQuery(id+"F6.wireOp",EDGE,"E7");Q4=makeQuery(id+"F23.opExtrude","CAP_EDGE",EDGE,{"disambiguationData":[OSD([subQ0]),TDD([makeQuery(id+"F6.imprint","IMPRINT",EDGE,{"disambiguationData":[TD([[makeQuery(id+"F6.imprint","INTERSECT",VERTEX,{"disambiguationData":[OD(0.0)],"derivedFrom":[subQ0,sQuery(id+"F6.wireOp",EDGE,"E10.left")]}),1.0]])],"derivedFrom":subQ0})])],"isStart":false});}
            var Q5;
            {var subQ0=sQuery(id+"F6.wireOp",EDGE,"E7");Q5=makeQuery(id+"F23.opExtrude","CAP_EDGE",EDGE,{"disambiguationData":[OSD([subQ0]),TDD([makeQuery(id+"F6.imprint","IMPRINT",EDGE,{"disambiguationData":[TD([[makeQuery(id+"F6.imprint","INTERSECT",VERTEX,{"disambiguationData":[OD(1.0)],"derivedFrom":[subQ0,sQuery(id+"F6.wireOp",EDGE,"E10.left")]}),-1.0]])],"derivedFrom":subQ0})])],"isStart":false});}
            var Q6;
            {var subQ0=sQuery(id+"F6.wireOp",EDGE,"E8");Q6=makeQuery(id+"F23.opExtrude","CAP_EDGE",EDGE,{"disambiguationData":[OSD([subQ0]),TDD([makeQuery(id+"F6.imprint","IMPRINT",EDGE,{"disambiguationData":[TD([[makeQuery(id+"F6.imprint","INTERSECT",VERTEX,{"disambiguationData":[OD(1.0)],"derivedFrom":[subQ0,sQuery(id+"F6.wireOp",EDGE,"E10.top")]}),-1.0]])],"derivedFrom":subQ0})])],"isStart":false});}
            var Q7;
            {var subQ0=sQuery(id+"F6.wireOp",EDGE,"E8");Q7=makeQuery(id+"F23.opExtrude","CAP_EDGE",EDGE,{"disambiguationData":[OSD([subQ0]),TDD([makeQuery(id+"F6.imprint","IMPRINT",EDGE,{"disambiguationData":[TD([[makeQuery(id+"F6.imprint","INTERSECT",VERTEX,{"disambiguationData":[OD(0.0)],"derivedFrom":[subQ0,sQuery(id+"F6.wireOp",EDGE,"E10.top")]}),1.0]])],"derivedFrom":subQ0})])],"isStart":false});}
            fillet(context, id + "F29", {"entities" : qUnion([Q0, Q1, Q2, Q3, Q4, Q5, Q6, Q7]), "radius" : 5 * mm, "tangentPropagation" : true, "allowEdgeOverflow" : false});
        }
        {
            var Q0;
            {var subQ0=sQuery(id+"F0.wireOp",EDGE,"E0.right");var subQ1=sQuery(id+"F0.wireOp",EDGE,"E0.top");var subQ2=makeQuery(id+"F0.imprint","INTERSECT",VERTEX,{"derivedFrom":[subQ1,subQ0]});Q0=makeQuery(id+"F0.imprint","IMPRINT",FACE,{"disambiguationData":[TD([[makeQuery(id+"F0.imprint","IMPRINT",EDGE,{"disambiguationData":[TD([[subQ2,1.0]])],"derivedFrom":subQ1}),1.0]])]});}
            var Q1;
            {var subQ0=sQuery(id+"F0.wireOp",EDGE,"E0.right");var subQ1=sQuery(id+"F0.wireOp",EDGE,"E0.top");var subQ2=makeQuery(id+"F0.imprint","INTERSECT",VERTEX,{"derivedFrom":[subQ1,subQ0]});Q1=makeQuery(id+"F0.imprint","IMPRINT",FACE,{"disambiguationData":[TD([[makeQuery(id+"F0.imprint","IMPRINT",EDGE,{"disambiguationData":[TD([[subQ2,1.0]])],"derivedFrom":subQ1}),-1.0]])]});}
            extrude(context, id + "F30", {"entities" : qUnion([Q0, Q1]), "operationType" : NewBodyOperationType.INTERSECT, "oppositeDirection" : true, "depth" : 26.75 * mm});
        }
    });
